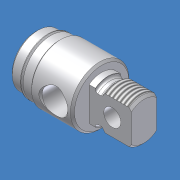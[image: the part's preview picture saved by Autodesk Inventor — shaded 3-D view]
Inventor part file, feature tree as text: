
AUTODESK INVENTOR PART (.ipt)
format: ipt  version: 2012 (Build 160160000, 160)  size: 266,240 bytes
history: native  units: mm (DEFAULTED — no unit token found)
features: other x155, sketch x7, revolve x5, extrude x2, thread x1
ambient origin geometry x8: Origin, YZ Plane, XZ Plane, XY Plane, X Axis, Y Axis, Z Axis, Center Point
bodies: Solid1 (feature_tree)
feature tree (170):
  other  "04P0010_rear_head"
  revolve  "Revolution1"  Angle=360.0deg
  revolve  "Revolution2"  [1 undecoded]
  thread  "Thread1"  [1 undecoded]
  extrude  "Extrusion1"  TaperAngle=360.0deg  [1 undecoded]
  revolve  "Revolution3"  [1 undecoded]
  revolve  "Revolution4"  [1 undecoded]
  revolve  "Revolution5"  [1 undecoded]
  extrude  "Extrusion2"  [1 undecoded]
  other  "c1_XY"
  other  "c1_YZ"
  other  "c1_ZX"
  other  "c1_X"
  other  "c1_Y"
  other  "c1_Z"
  other  "c1_Center"
  other  "cc1_XY"
  other  "cc1_YZ"
  other  "cc1_ZX"
  other  "cc1_X"
  other  "cc1_Y"
  other  "cc1_Z"
  other  "cc1_Center"
  other  "c2_XY"
  other  "c2_YZ"
  other  "c2_ZX"
  other  "c2_X"
  other  "c2_Y"
  other  "c2_Z"
  other  "c2_Center"
  other  "cc2_XY"
  other  "cc2_YZ"
  other  "cc2_ZX"
  other  "cc2_X"
  other  "cc2_Y"
  other  "cc2_Z"
  other  "cc2_Center"
  other  "to_tube_XY"
  other  "to_tube_YZ"
  other  "to_tube_ZX"
  other  "to_tube_X"
  other  "to_tube_Y"
  other  "to_tube_Z"
  other  "to_tube_Center"
  other  "to_nut_XY"
  other  "to_nut_YZ"
  other  "to_nut_ZX"
  other  "to_nut_X"
  other  "to_nut_Y"
  other  "to_nut_Z"
  other  "to_nut_Center"
  other  "lovra1_XY"
  other  "lovra1_YZ"
  other  "lovra1_ZX"
  other  "lovra1_X"
  other  "lovra1_Y"
  other  "lovra1_Z"
  other  "lovra1_Center"
  other  "lovra2_XY"
  other  "lovra2_YZ"
  other  "lovra2_ZX"
  other  "lovra2_X"
  other  "lovra2_Y"
  other  "lovra2_Z"
  other  "lovra2_Center"
  other  "lovra3_XY"
  other  "lovra3_YZ"
  other  "lovra3_ZX"
  other  "lovra3_X"
  other  "lovra3_Y"
  other  "lovra3_Z"
  other  "lovra3_Center"
  other  "to_pin_XY"
  other  "to_pin_YZ"
  other  "to_pin_ZX"
  other  "to_pin_X"
  other  "to_pin_Y"
  other  "to_pin_Z"
  other  "to_pin_Center"
  other  "olen_XY"
  other  "olen_YZ"
  other  "olen_ZX"
  other  "olen_X"
  other  "olen_Y"
  other  "olen_Z"
  other  "olen_Center"
  other  "thd1_XY"
  other  "thd1_YZ"
  other  "thd1_ZX"
  other  "thd1_X"
  other  "thd1_Y"
  other  "thd1_Z"
  other  "thd1_Center"
  other  "p1_XY"
  other  "p1_YZ"
  other  "p1_ZX"
  other  "p1_X"
  other  "p1_Y"
  other  "p1_Z"
  other  "p1_Center"
  other  "thd2_XY"
  other  "thd2_YZ"
  other  "thd2_ZX"
  other  "thd2_X"
  other  "thd2_Y"
  other  "thd2_Z"
  other  "thd2_Center"
  other  "p2_XY"
  other  "p2_YZ"
  other  "p2_ZX"
  other  "p2_X"
  other  "p2_Y"
  other  "p2_Z"
  other  "p2_Center"
  other  "port2_XY"
  other  "port2_YZ"
  other  "port2_ZX"
  other  "port2_X"
  other  "port2_Y"
  other  "port2_Z"
  other  "port2_Center"
  other  "port_XY"
  other  "port_YZ"
  other  "port_ZX"
  other  "port_X"
  other  "port_Y"
  other  "port_Z"
  other  "port_Center"
  other  "1_XY"
  other  "1_YZ"
  other  "1_ZX"
  other  "1_X"
  other  "1_Y"
  other  "1_Z"
  other  "1_Center"
  other  "lovra21_XY"
  other  "lovra21_YZ"
  other  "lovra21_ZX"
  other  "lovra21_X"
  other  "lovra21_Y"
  other  "lovra21_Z"
  other  "lovra21_Center"
  other  "lovra22_XY"
  other  "lovra22_YZ"
  other  "lovra22_ZX"
  other  "lovra22_X"
  other  "lovra22_Y"
  other  "lovra22_Z"
  other  "lovra22_Center"
  other  "to_screw_XY"
  other  "to_screw_YZ"
  other  "to_screw_ZX"
  other  "to_screw_X"
  other  "to_screw_Y"
  other  "to_screw_Z"
  other  "to_screw_Center"
  other  "to_mounting_bracket_XY"
  other  "to_mounting_bracket_YZ"
  other  "to_mounting_bracket_ZX"
  other  "to_mounting_bracket_X"
  other  "to_mounting_bracket_Y"
  other  "to_mounting_bracket_Z"
  other  "to_mounting_bracket_Center"
  sketch  "Sketch_8"  dims[d0=360.0deg d1=360.0deg]
  sketch  "Sketch_15"  dims[d9=14.19225mm d10=0.0mm]
  sketch  "Sketch_9"  dims[d2=9.008135mm d3=0.0mm d4=15.875mm d5=0.0mm d6=360.0deg]
  sketch  "Sketch_13"  dims[d7=360.0deg d8=360.0deg]
  sketch  "Sketch_19"
  sketch  "Sketch_24"
  sketch  "Sketch_43"
note: 7 required parameter values undecoded (feature->parameter linkage not recoverable at this tier; creation-order binding heuristic only, values carry confidence <= 0.55)